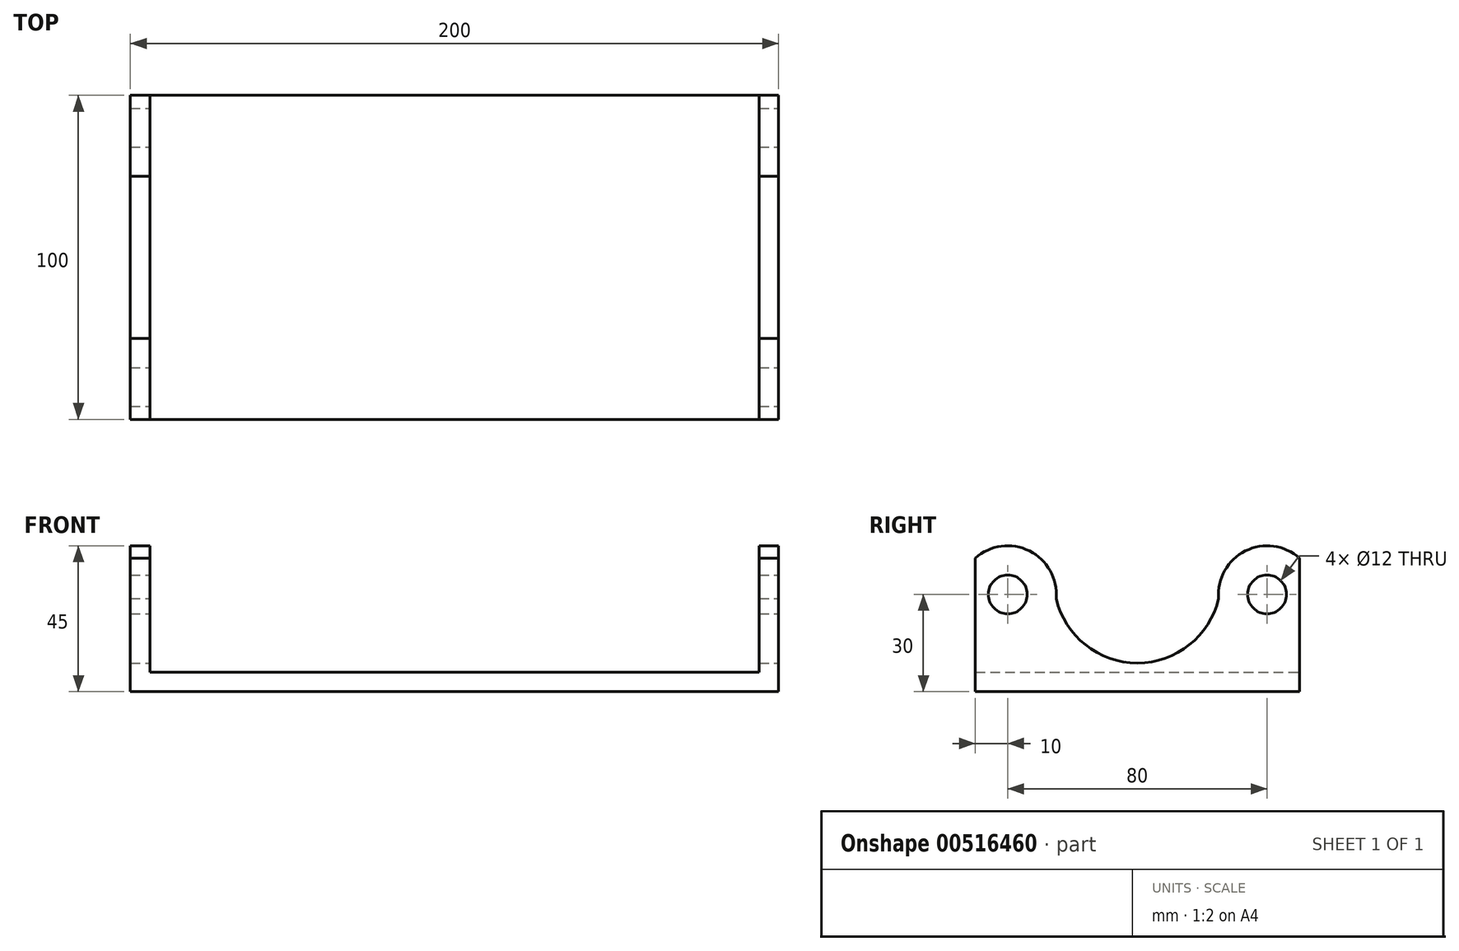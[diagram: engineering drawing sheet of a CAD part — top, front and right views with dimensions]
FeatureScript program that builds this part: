
annotation { "Feature Type Name" : "Feature", "Feature Type Description" : "" }
export const myFeature = defineFeature(function(context is Context, id is Id, definition is map)
    precondition{}
    {
        {
            var Q0;
            Q0=qCreatedBy(makeId("Front.planeOp"),FACE);
            var sketch = newSketch(context, id + "F0", { "sketchPlane" : qUnion([Q0])});
            skLineSegment(sketch, "E0", {"start": v(-63.5, 33.29) * mm, "end": v(-63.5, -16.71) * mm});
            skLineSegment(sketch, "E1", {"start": v(-63.5, -16.71) * mm, "end": v(136.5, -16.71) * mm});
            skLineSegment(sketch, "E2", {"start": v(136.5, -16.71) * mm, "end": v(136.5, 33.29) * mm});
            skLineSegment(sketch, "E3.0", {"start": v(130.5, -10.71) * mm, "end": v(130.5, 33.29) * mm});
            skLineSegment(sketch, "E3.1", {"start": v(-57.5, -10.71) * mm, "end": v(130.5, -10.71) * mm});
            skLineSegment(sketch, "E3.2", {"start": v(-57.5, 33.29) * mm, "end": v(-57.5, -10.71) * mm});
            skLineSegment(sketch, "E4", {"start": v(-63.5, 33.29) * mm, "end": v(-57.5, 33.29) * mm});
            skLineSegment(sketch, "E5", {"start": v(130.5, 33.29) * mm, "end": v(136.5, 33.29) * mm});
            skSolve(sketch);
        }
        {
            var Q0;
            Q0=makeQuery(id+"F0.imprint","IMPRINT",FACE,{"disambiguationData":[TD([[makeQuery(id+"F0.imprint","IMPRINT",EDGE,{"derivedFrom":sQuery(id+"F0.wireOp",EDGE,"E0")}),1.0]])]});
            extrude(context, id + "F1", {"entities" : qUnion([Q0]), "depth" : 100 * mm, "offsetDistance" : 25 * mm});
        }
        {
            var Q0;
            Q0=makeQuery(id+"F1.opExtrude","SWEPT_FACE",FACE,{"disambiguationData":[OSD([sQuery(id+"F0.wireOp",EDGE,"E2")])]});
            var sketch = newSketch(context, id + "F2", { "sketchPlane" : qUnion([Q0])});
            skLineSegment(sketch, "E6.0", {"start": v(-75, 13.29) * mm, "end": v(0, 13.29) * mm, "construction": true});
            skLineSegment(sketch, "E7.0", {"start": v(-90, -16.71) * mm, "end": v(-90, 33.29) * mm, "construction": true});
            skLineSegment(sketch, "E8.0", {"start": v(-10, -16.71) * mm, "end": v(-10, 33.29) * mm, "construction": true});
            skCircle(sketch, "E9", {"center": v(-90, 13.29) * mm, "radius": 6 * mm});
            skCircle(sketch, "E10", {"center": v(-10, 13.29) * mm, "radius": 6 * mm});
            skSolve(sketch);
        }
        {
            var Q0;
            Q0=makeQuery(id+"F2.imprint","IMPRINT",FACE,{"disambiguationData":[TD([[makeQuery(id+"F2.imprint","IMPRINT",EDGE,{"derivedFrom":sQuery(id+"F2.wireOp",EDGE,"E9")}),1.0]])]});
            var Q1;
            Q1=makeQuery(id+"F2.imprint","IMPRINT",FACE,{"disambiguationData":[TD([[makeQuery(id+"F2.imprint","IMPRINT",EDGE,{"derivedFrom":sQuery(id+"F2.wireOp",EDGE,"E10")}),1.0]])]});
            extrude(context, id + "F3", {"entities" : qUnion([Q0, Q1]), "operationType" : NewBodyOperationType.REMOVE, "endBound" : BoundingType.THROUGH_ALL, "oppositeDirection" : true, "depth" : 25 * mm, "offsetDistance" : 25 * mm});
        }
        {
            var Q0;
            Q0=makeQuery(id+"F1.opExtrude","SWEPT_FACE",FACE,{"disambiguationData":[OSD([sQuery(id+"F0.wireOp",EDGE,"E2")])]});
            var sketch = newSketch(context, id + "F4", { "sketchPlane" : qUnion([Q0])});
            skCircle(sketch, "E11", {"center": v(-90, 13.29) * mm, "radius": 15 * mm});
            skCircle(sketch, "E12", {"center": v(-10, 13.29) * mm, "radius": 15 * mm});
            skArc(sketch, "E13", {"start": v(-75.7, 17.85) * mm, "mid": v(-50, -7.86) * mm, "end": v(-24.3, 17.85) * mm});
            skSolve(sketch);
        }
        {
            var Q0;
            {var subQ3=sQuery(id+"F0.wireOp",EDGE,"E2");var subQ10=makeQuery(id+"F1.opExtrude","SWEPT_EDGE",EDGE,{"disambiguationData":[OSD([subQ3,sQuery(id+"F0.wireOp",EDGE,"E5")])]});Q0=makeQuery(id+"F4.imprint","IMPRINT",FACE,{"disambiguationData":[TD([[makeQuery(id+"F4.imprint","IMPRINT",EDGE,{"derivedFrom":subQ10}),-1.0]])]});}
            extrude(context, id + "F5", {"entities" : qUnion([Q0]), "operationType" : NewBodyOperationType.REMOVE, "endBound" : BoundingType.THROUGH_ALL, "oppositeDirection" : true, "depth" : 25 * mm, "offsetDistance" : 25 * mm});
        }
    });
